# Revit family: Faucet-Bidet-KOHLER-Pinstripe_Pure-K-13142
name_source: partatom
category: Plumbing Fixtures
revit_build: Autodesk Revit 2017 (Build: 20160225_1515(x64)
units: mm (PartAtom-declared; Revit-internal decimal feet)

## family parameters
Cut with Voids When Loaded = No
Host = Face
OmniClass Number = 23.31.11.00
OmniClass Title = Faucets
Part Type = Normal
Room Calculation Point = No
Round Connector Dimension = Use Diameter
Shared = No

## types (3) — shared parameters
ADA Compliant = No
Assembly Code = D2010
CW Connection = Yes
Cold Water Inlet = Cold Water Inlet
Date Modified = 03/23/2020
Default Elevation = 36"
Description = Vertical spray bidet faucet with lever handles
Drain Included = Yes
Flow Rate = 0 GPM
HW Connection = Yes
Handle Clearance = 2 3/4"
Height = 6 1/8"
Hot Water Inlet = Hot Water Inlet
Length = 2 1/8"
Manufacturer = KOHLER Co.
Master Format 2014 = 22 41 39
Master Format 2014 Name = Residential Faucets, Supplies, and Trim
Material = Premium Metal construction
Pressure = 0.00 psi
Product Documentation Link = https://www.us.kohler.com
Product Name = Pinstripe Pure
Product Page URL = http://www.us.kohler.com
Spout Reach = 0"
URL = https://www.us.kohler.com
Vent Connection = No
Waste Connection = No
Waste Water Outlet = Waste Water Outlet
WaterSense Certified = No

## per-type parameters (varying)
| type | Finish | Model | Type |
| CP-Polished Chrome | Kohler-Metal-CP-Polished_Chrome | K-13142-4A-CP | 1 |
| SN-Vibrant Polished Nickel | Kohler-Metal-SN-Vibrant_Polished_Nickel | K-13142-4A-SN | 2 |
| BN-Vibrant Brushed Nickel | Kohler-Metal-BN-Vibrant_Brushed_Nickel | K-13142-4A-BN | 3 |

## geometry (parser evidence)
native form markers: Sweep x11
no freeform markers — native parametric forms only
